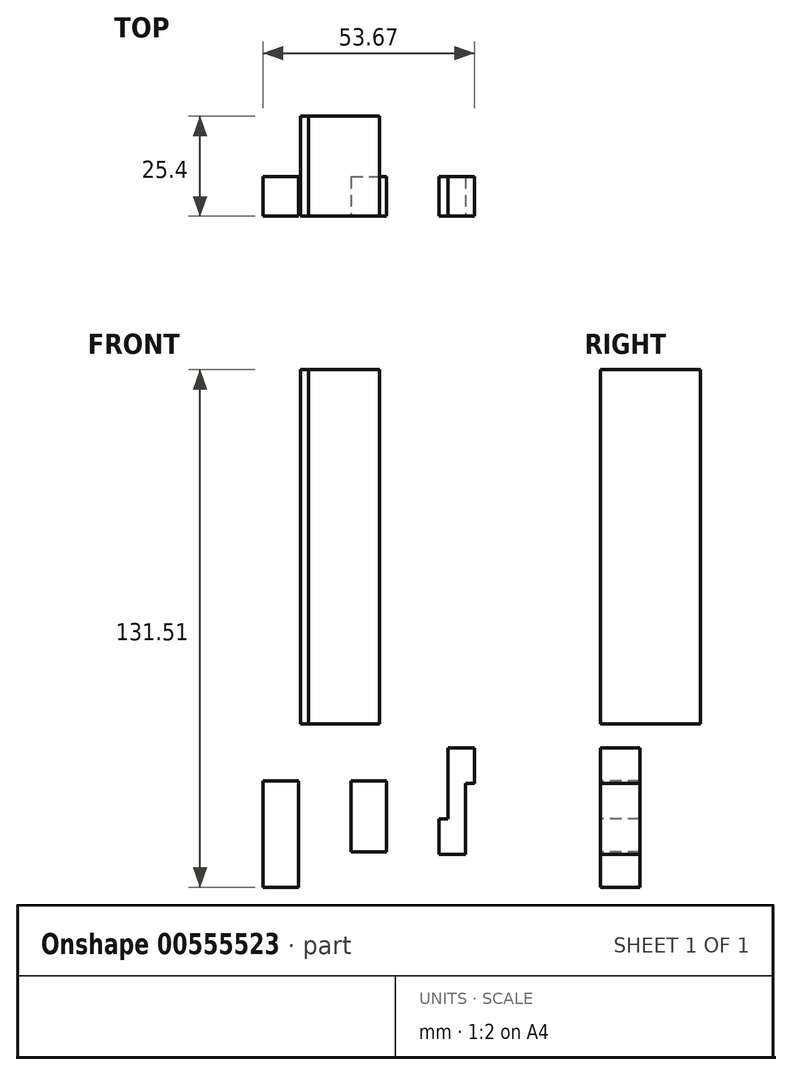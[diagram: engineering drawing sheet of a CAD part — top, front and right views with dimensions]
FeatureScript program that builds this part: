
annotation { "Feature Type Name" : "Feature", "Feature Type Description" : "" }
export const myFeature = defineFeature(function(context is Context, id is Id, definition is map)
    precondition{}
    {
        {
            var Q0;
            Q0=qCreatedBy(makeId("Front.planeOp"),FACE);
            var sketch = newSketch(context, id + "F0", { "sketchPlane" : qUnion([Q0])});
            skLineSegment(sketch, "E0.bottom", {"start": v(15.33, -10.42) * mm, "end": v(24.33, -10.42) * mm});
            skLineSegment(sketch, "E0.top", {"start": v(15.33, -37.42) * mm, "end": v(24.33, -37.42) * mm});
            skLineSegment(sketch, "E0.left", {"start": v(15.33, -10.42) * mm, "end": v(15.33, -37.42) * mm});
            skLineSegment(sketch, "E0.right", {"start": v(24.33, -10.42) * mm, "end": v(24.33, -37.42) * mm});
            skLineSegment(sketch, "E1.0", {"start": v(15.78, -10.42) * mm, "end": v(15.78, -37.42) * mm, "construction": true});
            skLineSegment(sketch, "E2.0", {"start": v(16.23, -10.42) * mm, "end": v(16.23, -37.42) * mm, "construction": true});
            skLineSegment(sketch, "E3.0", {"start": v(16.68, -10.42) * mm, "end": v(16.68, -37.42) * mm, "construction": true});
            skLineSegment(sketch, "E4.0", {"start": v(17.13, -10.42) * mm, "end": v(17.13, -37.42) * mm, "construction": true});
            skLineSegment(sketch, "E5.0", {"start": v(17.58, -10.42) * mm, "end": v(17.58, -37.42) * mm, "construction": true});
            skLineSegment(sketch, "E6.0", {"start": v(18.03, -10.42) * mm, "end": v(18.03, -37.42) * mm, "construction": true});
            skLineSegment(sketch, "E7.0", {"start": v(18.48, -10.42) * mm, "end": v(18.48, -37.42) * mm, "construction": true});
            skLineSegment(sketch, "E8.0", {"start": v(18.93, -10.42) * mm, "end": v(18.93, -37.42) * mm, "construction": true});
            skLineSegment(sketch, "E9.0", {"start": v(19.38, -10.42) * mm, "end": v(19.38, -37.42) * mm, "construction": true});
            skLineSegment(sketch, "E10.0", {"start": v(19.83, -10.42) * mm, "end": v(19.83, -37.42) * mm, "construction": true});
            skLineSegment(sketch, "E11.0", {"start": v(20.28, -10.42) * mm, "end": v(20.28, -37.42) * mm, "construction": true});
            skLineSegment(sketch, "E12.0", {"start": v(20.73, -10.42) * mm, "end": v(20.73, -37.42) * mm, "construction": true});
            skLineSegment(sketch, "E13.0", {"start": v(21.18, -10.42) * mm, "end": v(21.18, -37.42) * mm, "construction": true});
            skLineSegment(sketch, "E14.0", {"start": v(21.63, -10.42) * mm, "end": v(21.63, -37.42) * mm, "construction": true});
            skLineSegment(sketch, "E15.0", {"start": v(22.08, -10.42) * mm, "end": v(22.08, -37.42) * mm, "construction": true});
            skLineSegment(sketch, "E16.0", {"start": v(22.53, -10.42) * mm, "end": v(22.53, -37.42) * mm, "construction": true});
            skLineSegment(sketch, "E17.0", {"start": v(22.98, -10.42) * mm, "end": v(22.98, -37.42) * mm, "construction": true});
            skLineSegment(sketch, "E18.0", {"start": v(23.43, -10.42) * mm, "end": v(23.43, -37.42) * mm, "construction": true});
            skLineSegment(sketch, "E19.0", {"start": v(23.88, -10.42) * mm, "end": v(23.88, -37.42) * mm, "construction": true});
            skLineSegment(sketch, "E20.0", {"start": v(15.33, -36.97) * mm, "end": v(24.33, -36.97) * mm, "construction": true});
            skLineSegment(sketch, "E21.0", {"start": v(15.33, -36.52) * mm, "end": v(24.33, -36.52) * mm, "construction": true});
            skLineSegment(sketch, "E22.0", {"start": v(15.33, -36.07) * mm, "end": v(24.33, -36.07) * mm, "construction": true});
            skLineSegment(sketch, "E23.0", {"start": v(15.33, -35.62) * mm, "end": v(24.33, -35.62) * mm, "construction": true});
            skLineSegment(sketch, "E24.0", {"start": v(15.33, -35.17) * mm, "end": v(24.33, -35.17) * mm, "construction": true});
            skLineSegment(sketch, "E25.0", {"start": v(15.33, -34.72) * mm, "end": v(24.33, -34.72) * mm, "construction": true});
            skLineSegment(sketch, "E26.0", {"start": v(15.33, -34.27) * mm, "end": v(24.33, -34.27) * mm, "construction": true});
            skLineSegment(sketch, "E27.0", {"start": v(15.33, -33.82) * mm, "end": v(24.33, -33.82) * mm, "construction": true});
            skLineSegment(sketch, "E28.0", {"start": v(15.33, -33.37) * mm, "end": v(24.33, -33.37) * mm, "construction": true});
            skLineSegment(sketch, "E29.0", {"start": v(15.33, -32.92) * mm, "end": v(24.33, -32.92) * mm, "construction": true});
            skLineSegment(sketch, "E30.0", {"start": v(15.33, -32.47) * mm, "end": v(24.33, -32.47) * mm, "construction": true});
            skLineSegment(sketch, "E31.0", {"start": v(15.33, -32.02) * mm, "end": v(24.33, -32.02) * mm, "construction": true});
            skLineSegment(sketch, "E32.0", {"start": v(15.33, -31.57) * mm, "end": v(24.33, -31.57) * mm, "construction": true});
            skLineSegment(sketch, "E33.0", {"start": v(15.33, -31.12) * mm, "end": v(24.33, -31.12) * mm, "construction": true});
            skLineSegment(sketch, "E34.0", {"start": v(15.33, -30.67) * mm, "end": v(24.33, -30.67) * mm, "construction": true});
            skLineSegment(sketch, "E35.0", {"start": v(15.33, -30.22) * mm, "end": v(24.33, -30.22) * mm, "construction": true});
            skLineSegment(sketch, "E36.0", {"start": v(15.33, -29.77) * mm, "end": v(24.33, -29.77) * mm, "construction": true});
            skLineSegment(sketch, "E37.0", {"start": v(15.33, -29.32) * mm, "end": v(24.33, -29.32) * mm, "construction": true});
            skLineSegment(sketch, "E38.0", {"start": v(15.33, -28.87) * mm, "end": v(24.33, -28.87) * mm, "construction": true});
            skLineSegment(sketch, "E39.0", {"start": v(15.33, -28.42) * mm, "end": v(24.33, -28.42) * mm, "construction": true});
            skLineSegment(sketch, "E40.0", {"start": v(15.33, -27.97) * mm, "end": v(24.33, -27.97) * mm, "construction": true});
            skLineSegment(sketch, "E41.0", {"start": v(15.33, -27.52) * mm, "end": v(24.33, -27.52) * mm, "construction": true});
            skLineSegment(sketch, "E42.0", {"start": v(15.33, -27.07) * mm, "end": v(24.33, -27.07) * mm, "construction": true});
            skLineSegment(sketch, "E43.0", {"start": v(15.33, -26.62) * mm, "end": v(24.33, -26.62) * mm, "construction": true});
            skLineSegment(sketch, "E44.0", {"start": v(15.33, -26.17) * mm, "end": v(24.33, -26.17) * mm, "construction": true});
            skLineSegment(sketch, "E45.0", {"start": v(15.33, -25.72) * mm, "end": v(24.33, -25.72) * mm, "construction": true});
            skLineSegment(sketch, "E46.0", {"start": v(15.33, -25.27) * mm, "end": v(24.33, -25.27) * mm, "construction": true});
            skLineSegment(sketch, "E47.0", {"start": v(15.33, -24.82) * mm, "end": v(24.33, -24.82) * mm, "construction": true});
            skLineSegment(sketch, "E48.0", {"start": v(15.33, -24.37) * mm, "end": v(24.33, -24.37) * mm, "construction": true});
            skLineSegment(sketch, "E49.0", {"start": v(15.33, -23.92) * mm, "end": v(24.33, -23.92) * mm, "construction": true});
            skLineSegment(sketch, "E50.0", {"start": v(15.33, -23.47) * mm, "end": v(24.33, -23.47) * mm, "construction": true});
            skLineSegment(sketch, "E51.0", {"start": v(15.33, -23.02) * mm, "end": v(24.33, -23.02) * mm, "construction": true});
            skLineSegment(sketch, "E52.0", {"start": v(15.33, -22.57) * mm, "end": v(24.33, -22.57) * mm, "construction": true});
            skLineSegment(sketch, "E53.0", {"start": v(15.33, -22.12) * mm, "end": v(24.33, -22.12) * mm, "construction": true});
            skLineSegment(sketch, "E54.0", {"start": v(15.33, -21.67) * mm, "end": v(24.33, -21.67) * mm, "construction": true});
            skLineSegment(sketch, "E55.0", {"start": v(15.33, -21.22) * mm, "end": v(24.33, -21.22) * mm, "construction": true});
            skLineSegment(sketch, "E56.0", {"start": v(15.33, -20.77) * mm, "end": v(24.33, -20.77) * mm, "construction": true});
            skLineSegment(sketch, "E57.0", {"start": v(15.33, -20.32) * mm, "end": v(24.33, -20.32) * mm, "construction": true});
            skLineSegment(sketch, "E58.0", {"start": v(15.33, -19.87) * mm, "end": v(24.33, -19.87) * mm, "construction": true});
            skLineSegment(sketch, "E59.0", {"start": v(15.33, -19.42) * mm, "end": v(24.33, -19.42) * mm, "construction": true});
            skLineSegment(sketch, "E60.0", {"start": v(15.33, -18.97) * mm, "end": v(24.33, -18.97) * mm, "construction": true});
            skLineSegment(sketch, "E61.0", {"start": v(15.33, -18.52) * mm, "end": v(24.33, -18.52) * mm, "construction": true});
            skLineSegment(sketch, "E62.0", {"start": v(15.33, -18.07) * mm, "end": v(24.33, -18.07) * mm, "construction": true});
            skLineSegment(sketch, "E63.0", {"start": v(15.33, -17.62) * mm, "end": v(24.33, -17.62) * mm, "construction": true});
            skLineSegment(sketch, "E64.0", {"start": v(15.33, -17.17) * mm, "end": v(24.33, -17.17) * mm, "construction": true});
            skLineSegment(sketch, "E65.0", {"start": v(15.33, -16.72) * mm, "end": v(24.33, -16.72) * mm, "construction": true});
            skLineSegment(sketch, "E66.0", {"start": v(15.33, -16.27) * mm, "end": v(24.33, -16.27) * mm, "construction": true});
            skLineSegment(sketch, "E67.0", {"start": v(15.33, -15.82) * mm, "end": v(24.33, -15.82) * mm, "construction": true});
            skLineSegment(sketch, "E68.0", {"start": v(15.33, -15.37) * mm, "end": v(24.33, -15.37) * mm, "construction": true});
            skLineSegment(sketch, "E69.0", {"start": v(15.33, -14.92) * mm, "end": v(24.33, -14.92) * mm, "construction": true});
            skLineSegment(sketch, "E70.0", {"start": v(15.33, -14.47) * mm, "end": v(24.33, -14.47) * mm, "construction": true});
            skLineSegment(sketch, "E71.0", {"start": v(15.33, -14.02) * mm, "end": v(24.33, -14.02) * mm, "construction": true});
            skLineSegment(sketch, "E72.0", {"start": v(15.33, -13.57) * mm, "end": v(24.33, -13.57) * mm, "construction": true});
            skLineSegment(sketch, "E73.0", {"start": v(15.33, -13.12) * mm, "end": v(24.33, -13.12) * mm, "construction": true});
            skLineSegment(sketch, "E74.0", {"start": v(15.33, -12.67) * mm, "end": v(24.33, -12.67) * mm, "construction": true});
            skLineSegment(sketch, "E75.0", {"start": v(15.33, -12.22) * mm, "end": v(24.33, -12.22) * mm, "construction": true});
            skLineSegment(sketch, "E76.0", {"start": v(15.33, -11.77) * mm, "end": v(24.33, -11.77) * mm, "construction": true});
            skLineSegment(sketch, "E77.0", {"start": v(15.33, -11.32) * mm, "end": v(24.33, -11.32) * mm, "construction": true});
            skLineSegment(sketch, "E78.0", {"start": v(15.33, -10.87) * mm, "end": v(24.33, -10.87) * mm, "construction": true});
            skSolve(sketch);
        }
        {
            var Q0;
            Q0=makeQuery(id+"F0.imprint","IMPRINT",FACE,{"disambiguationData":[TD([[makeQuery(id+"F0.imprint","IMPRINT",EDGE,{"derivedFrom":sQuery(id+"F0.wireOp",EDGE,"E0.bottom")}),-1.0]])]});
            extrude(context, id + "F1", {"entities" : qUnion([Q0]), "oppositeDirection" : true, "depth" : 10 * mm, "offsetDistance" : 25.4 * mm});
        }
        {
            var Q0;
            Q0=qCreatedBy(makeId("Front.planeOp"),FACE);
            var sketch = newSketch(context, id + "F2", { "sketchPlane" : qUnion([Q0])});
            skLineSegment(sketch, "E79.top", {"start": v(37.66, -28.43) * mm, "end": v(46.66, -28.43) * mm});
            skLineSegment(sketch, "E80.0", {"start": v(38.11, -10.43) * mm, "end": v(38.11, -28.43) * mm, "construction": true});
            skLineSegment(sketch, "E81.0", {"start": v(38.56, -10.43) * mm, "end": v(38.56, -28.43) * mm, "construction": true});
            skLineSegment(sketch, "E82.0", {"start": v(39.01, -10.43) * mm, "end": v(39.01, -28.43) * mm, "construction": true});
            skLineSegment(sketch, "E83.0", {"start": v(39.46, -10.43) * mm, "end": v(39.46, -28.43) * mm, "construction": true});
            skLineSegment(sketch, "E84.0", {"start": v(39.91, -10.43) * mm, "end": v(39.91, -28.43) * mm, "construction": true});
            skLineSegment(sketch, "E85.0", {"start": v(40.36, -10.43) * mm, "end": v(40.36, -28.43) * mm, "construction": true});
            skLineSegment(sketch, "E86.0", {"start": v(40.81, -10.43) * mm, "end": v(40.81, -28.43) * mm, "construction": true});
            skLineSegment(sketch, "E87.0", {"start": v(41.26, -10.43) * mm, "end": v(41.26, -28.43) * mm, "construction": true});
            skLineSegment(sketch, "E88.0", {"start": v(41.71, -10.43) * mm, "end": v(41.71, -28.43) * mm, "construction": true});
            skLineSegment(sketch, "E89.0", {"start": v(42.16, -10.43) * mm, "end": v(42.16, -28.43) * mm, "construction": true});
            skLineSegment(sketch, "E90.0", {"start": v(42.61, -10.43) * mm, "end": v(42.61, -28.43) * mm, "construction": true});
            skLineSegment(sketch, "E91.0", {"start": v(43.06, -10.43) * mm, "end": v(43.06, -28.43) * mm, "construction": true});
            skLineSegment(sketch, "E92.0", {"start": v(43.51, -10.43) * mm, "end": v(43.51, -28.43) * mm, "construction": true});
            skLineSegment(sketch, "E93.0", {"start": v(43.96, -10.43) * mm, "end": v(43.96, -28.43) * mm, "construction": true});
            skLineSegment(sketch, "E94.0", {"start": v(44.41, -10.43) * mm, "end": v(44.41, -28.43) * mm, "construction": true});
            skLineSegment(sketch, "E95.0", {"start": v(44.86, -10.43) * mm, "end": v(44.86, -28.43) * mm, "construction": true});
            skLineSegment(sketch, "E96.0", {"start": v(45.31, -10.43) * mm, "end": v(45.31, -28.43) * mm, "construction": true});
            skLineSegment(sketch, "E97.0", {"start": v(45.76, -10.43) * mm, "end": v(45.76, -28.43) * mm, "construction": true});
            skLineSegment(sketch, "E98.0", {"start": v(46.21, -10.43) * mm, "end": v(46.21, -28.43) * mm, "construction": true});
            skLineSegment(sketch, "E99.0", {"start": v(37.66, -27.98) * mm, "end": v(46.66, -27.98) * mm, "construction": true});
            skLineSegment(sketch, "E100.0", {"start": v(37.66, -27.53) * mm, "end": v(46.66, -27.53) * mm, "construction": true});
            skLineSegment(sketch, "E101.0", {"start": v(37.66, -27.08) * mm, "end": v(46.66, -27.08) * mm, "construction": true});
            skLineSegment(sketch, "E102.0", {"start": v(37.66, -26.63) * mm, "end": v(46.66, -26.63) * mm, "construction": true});
            skLineSegment(sketch, "E103.0", {"start": v(37.66, -26.18) * mm, "end": v(46.66, -26.18) * mm, "construction": true});
            skLineSegment(sketch, "E104.0", {"start": v(37.66, -25.73) * mm, "end": v(46.66, -25.73) * mm, "construction": true});
            skLineSegment(sketch, "E105.0", {"start": v(37.66, -25.28) * mm, "end": v(46.66, -25.28) * mm, "construction": true});
            skLineSegment(sketch, "E106.0", {"start": v(37.66, -24.83) * mm, "end": v(46.66, -24.83) * mm, "construction": true});
            skLineSegment(sketch, "E107.0", {"start": v(37.66, -24.38) * mm, "end": v(46.66, -24.38) * mm, "construction": true});
            skLineSegment(sketch, "E108.0", {"start": v(37.66, -23.93) * mm, "end": v(46.66, -23.93) * mm, "construction": true});
            skLineSegment(sketch, "E109.0", {"start": v(37.66, -23.48) * mm, "end": v(46.66, -23.48) * mm, "construction": true});
            skLineSegment(sketch, "E110.0", {"start": v(37.66, -23.03) * mm, "end": v(46.66, -23.03) * mm, "construction": true});
            skLineSegment(sketch, "E111.0", {"start": v(37.66, -22.58) * mm, "end": v(46.66, -22.58) * mm, "construction": true});
            skLineSegment(sketch, "E112.0", {"start": v(37.66, -22.13) * mm, "end": v(46.66, -22.13) * mm, "construction": true});
            skLineSegment(sketch, "E113.0", {"start": v(37.66, -21.68) * mm, "end": v(46.66, -21.68) * mm, "construction": true});
            skLineSegment(sketch, "E114.0", {"start": v(37.66, -21.23) * mm, "end": v(46.66, -21.23) * mm, "construction": true});
            skLineSegment(sketch, "E115.0", {"start": v(37.66, -20.78) * mm, "end": v(46.66, -20.78) * mm, "construction": true});
            skLineSegment(sketch, "E116.0", {"start": v(37.66, -20.33) * mm, "end": v(46.66, -20.33) * mm, "construction": true});
            skLineSegment(sketch, "E117.0", {"start": v(37.66, -19.88) * mm, "end": v(46.66, -19.88) * mm, "construction": true});
            skLineSegment(sketch, "E118.0", {"start": v(37.66, -19.43) * mm, "end": v(46.66, -19.43) * mm, "construction": true});
            skLineSegment(sketch, "E119.0", {"start": v(37.66, -18.98) * mm, "end": v(46.66, -18.98) * mm, "construction": true});
            skLineSegment(sketch, "E120.0", {"start": v(37.66, -18.53) * mm, "end": v(46.66, -18.53) * mm, "construction": true});
            skLineSegment(sketch, "E121.0", {"start": v(37.66, -18.08) * mm, "end": v(46.66, -18.08) * mm, "construction": true});
            skLineSegment(sketch, "E122.0", {"start": v(37.66, -17.63) * mm, "end": v(46.66, -17.63) * mm, "construction": true});
            skLineSegment(sketch, "E123.0", {"start": v(37.66, -17.18) * mm, "end": v(46.66, -17.18) * mm, "construction": true});
            skLineSegment(sketch, "E124.0", {"start": v(37.66, -16.73) * mm, "end": v(46.66, -16.73) * mm, "construction": true});
            skLineSegment(sketch, "E125.0", {"start": v(37.66, -16.28) * mm, "end": v(46.66, -16.28) * mm, "construction": true});
            skLineSegment(sketch, "E126.0", {"start": v(37.66, -15.83) * mm, "end": v(46.66, -15.83) * mm, "construction": true});
            skLineSegment(sketch, "E127.0", {"start": v(37.66, -15.38) * mm, "end": v(46.66, -15.38) * mm, "construction": true});
            skLineSegment(sketch, "E128.0", {"start": v(37.66, -14.93) * mm, "end": v(46.66, -14.93) * mm, "construction": true});
            skLineSegment(sketch, "E129.0", {"start": v(37.66, -14.48) * mm, "end": v(46.66, -14.48) * mm, "construction": true});
            skLineSegment(sketch, "E130.0", {"start": v(37.66, -14.03) * mm, "end": v(46.66, -14.03) * mm, "construction": true});
            skLineSegment(sketch, "E131.0", {"start": v(37.66, -13.58) * mm, "end": v(46.66, -13.58) * mm, "construction": true});
            skLineSegment(sketch, "E132.0", {"start": v(37.66, -13.13) * mm, "end": v(46.66, -13.13) * mm, "construction": true});
            skLineSegment(sketch, "E133.0", {"start": v(37.66, -12.68) * mm, "end": v(46.66, -12.68) * mm, "construction": true});
            skLineSegment(sketch, "E134.0", {"start": v(37.66, -12.23) * mm, "end": v(46.66, -12.23) * mm, "construction": true});
            skLineSegment(sketch, "E135.0", {"start": v(37.66, -11.78) * mm, "end": v(46.66, -11.78) * mm, "construction": true});
            skLineSegment(sketch, "E136.0", {"start": v(37.66, -11.33) * mm, "end": v(46.66, -11.33) * mm, "construction": true});
            skLineSegment(sketch, "E137.0", {"start": v(37.66, -10.88) * mm, "end": v(46.66, -10.88) * mm, "construction": true});
            skLineSegment(sketch, "E138.0", {"start": v(37.66, -10.43) * mm, "end": v(46.66, -10.43) * mm});
            skLineSegment(sketch, "E139", {"start": v(37.66, -28.43) * mm, "end": v(37.66, -10.43) * mm});
            skLineSegment(sketch, "E140", {"start": v(46.66, -10.43) * mm, "end": v(46.66, -28.43) * mm});
            skSolve(sketch);
        }
        {
            var Q0;
            Q0 = qSketchRegion(id + "F2", true);
            extrude(context, id + "F3", {"entities" : qUnion([Q0]), "oppositeDirection" : true, "depth" : 10 * mm, "offsetDistance" : 25.4 * mm});
        }
        {
            var Q0;
            Q0=qCreatedBy(makeId("Front.planeOp"),FACE);
            var sketch = newSketch(context, id + "F4", { "sketchPlane" : qUnion([Q0])});
            skLineSegment(sketch, "E141.0", {"start": v(62.25, -2.04) * mm, "end": v(62.25, -29.04) * mm, "construction": true});
            skLineSegment(sketch, "E142.0", {"start": v(62.7, -2.04) * mm, "end": v(62.7, -29.04) * mm, "construction": true});
            skLineSegment(sketch, "E143.0", {"start": v(63.15, -2.04) * mm, "end": v(63.15, -29.04) * mm, "construction": true});
            skLineSegment(sketch, "E144.0", {"start": v(63.6, -2.04) * mm, "end": v(63.6, -29.04) * mm, "construction": true});
            skLineSegment(sketch, "E145.0", {"start": v(64.05, -2.04) * mm, "end": v(64.05, -29.04) * mm, "construction": true});
            skLineSegment(sketch, "E146.0", {"start": v(64.5, -2.04) * mm, "end": v(64.5, -29.04) * mm, "construction": true});
            skLineSegment(sketch, "E147.0", {"start": v(64.95, -2.04) * mm, "end": v(64.95, -29.04) * mm, "construction": true});
            skLineSegment(sketch, "E148.0", {"start": v(65.4, -2.04) * mm, "end": v(65.4, -29.04) * mm, "construction": true});
            skLineSegment(sketch, "E149.0", {"start": v(65.85, -2.04) * mm, "end": v(65.85, -29.04) * mm, "construction": true});
            skLineSegment(sketch, "E150.0", {"start": v(66.3, -2.04) * mm, "end": v(66.3, -29.04) * mm, "construction": true});
            skLineSegment(sketch, "E151.0", {"start": v(66.75, -2.04) * mm, "end": v(66.75, -29.04) * mm, "construction": true});
            skLineSegment(sketch, "E152.0", {"start": v(67.2, -2.04) * mm, "end": v(67.2, -11.04) * mm, "construction": true});
            skLineSegment(sketch, "E153.0", {"start": v(67.65, -2.04) * mm, "end": v(67.65, -11.04) * mm, "construction": true});
            skLineSegment(sketch, "E154.0", {"start": v(68.1, -2.04) * mm, "end": v(68.1, -11.04) * mm, "construction": true});
            skLineSegment(sketch, "E155.0", {"start": v(68.55, -2.04) * mm, "end": v(68.55, -11.04) * mm, "construction": true});
            skLineSegment(sketch, "E156.0", {"start": v(60, -28.59) * mm, "end": v(66.75, -28.59) * mm, "construction": true});
            skLineSegment(sketch, "E157.0", {"start": v(60, -28.14) * mm, "end": v(66.75, -28.14) * mm, "construction": true});
            skLineSegment(sketch, "E158.0", {"start": v(60, -27.69) * mm, "end": v(66.75, -27.69) * mm, "construction": true});
            skLineSegment(sketch, "E159.0", {"start": v(60, -27.24) * mm, "end": v(66.75, -27.24) * mm, "construction": true});
            skLineSegment(sketch, "E160.0", {"start": v(60, -26.79) * mm, "end": v(66.75, -26.79) * mm, "construction": true});
            skLineSegment(sketch, "E161.0", {"start": v(60, -26.34) * mm, "end": v(66.75, -26.34) * mm, "construction": true});
            skLineSegment(sketch, "E162.0", {"start": v(60, -25.89) * mm, "end": v(66.75, -25.89) * mm, "construction": true});
            skLineSegment(sketch, "E163.0", {"start": v(60, -25.44) * mm, "end": v(66.75, -25.44) * mm, "construction": true});
            skLineSegment(sketch, "E164.0", {"start": v(60, -24.99) * mm, "end": v(66.75, -24.99) * mm, "construction": true});
            skLineSegment(sketch, "E165.0", {"start": v(60, -24.54) * mm, "end": v(66.75, -24.54) * mm, "construction": true});
            skLineSegment(sketch, "E166.0", {"start": v(60, -24.09) * mm, "end": v(66.75, -24.09) * mm, "construction": true});
            skLineSegment(sketch, "E167.0", {"start": v(60, -23.64) * mm, "end": v(66.75, -23.64) * mm, "construction": true});
            skLineSegment(sketch, "E168.0", {"start": v(60, -23.19) * mm, "end": v(66.75, -23.19) * mm, "construction": true});
            skLineSegment(sketch, "E169.0", {"start": v(60, -22.74) * mm, "end": v(66.75, -22.74) * mm, "construction": true});
            skLineSegment(sketch, "E170.0", {"start": v(60, -22.29) * mm, "end": v(66.75, -22.29) * mm, "construction": true});
            skLineSegment(sketch, "E171.0", {"start": v(60, -21.84) * mm, "end": v(66.75, -21.84) * mm, "construction": true});
            skLineSegment(sketch, "E172.0", {"start": v(60, -21.39) * mm, "end": v(66.75, -21.39) * mm, "construction": true});
            skLineSegment(sketch, "E173.0", {"start": v(60, -20.94) * mm, "end": v(66.75, -20.94) * mm, "construction": true});
            skLineSegment(sketch, "E174.0", {"start": v(60, -20.49) * mm, "end": v(66.75, -20.49) * mm, "construction": true});
            skLineSegment(sketch, "E175.0", {"start": v(60, -20.04) * mm, "end": v(66.75, -20.04) * mm, "construction": true});
            skLineSegment(sketch, "E176.0", {"start": v(62.25, -19.59) * mm, "end": v(66.75, -19.59) * mm, "construction": true});
            skLineSegment(sketch, "E177.0", {"start": v(62.25, -19.14) * mm, "end": v(66.75, -19.14) * mm, "construction": true});
            skLineSegment(sketch, "E178.0", {"start": v(62.25, -18.69) * mm, "end": v(66.75, -18.69) * mm, "construction": true});
            skLineSegment(sketch, "E179.0", {"start": v(62.25, -18.24) * mm, "end": v(66.75, -18.24) * mm, "construction": true});
            skLineSegment(sketch, "E180.0", {"start": v(62.25, -17.79) * mm, "end": v(66.75, -17.79) * mm, "construction": true});
            skLineSegment(sketch, "E181.0", {"start": v(62.25, -17.34) * mm, "end": v(66.75, -17.34) * mm, "construction": true});
            skLineSegment(sketch, "E182.0", {"start": v(62.25, -16.89) * mm, "end": v(66.75, -16.89) * mm, "construction": true});
            skLineSegment(sketch, "E183.0", {"start": v(62.25, -16.44) * mm, "end": v(66.75, -16.44) * mm, "construction": true});
            skLineSegment(sketch, "E184.0", {"start": v(62.25, -15.99) * mm, "end": v(66.75, -15.99) * mm, "construction": true});
            skLineSegment(sketch, "E185.0", {"start": v(62.25, -15.54) * mm, "end": v(66.75, -15.54) * mm, "construction": true});
            skLineSegment(sketch, "E186.0", {"start": v(62.25, -15.09) * mm, "end": v(66.75, -15.09) * mm, "construction": true});
            skLineSegment(sketch, "E187.0", {"start": v(62.25, -14.64) * mm, "end": v(66.75, -14.64) * mm, "construction": true});
            skLineSegment(sketch, "E188.0", {"start": v(62.25, -14.19) * mm, "end": v(66.75, -14.19) * mm, "construction": true});
            skLineSegment(sketch, "E189.0", {"start": v(62.25, -13.74) * mm, "end": v(66.75, -13.74) * mm, "construction": true});
            skLineSegment(sketch, "E190.0", {"start": v(62.25, -13.29) * mm, "end": v(66.75, -13.29) * mm, "construction": true});
            skLineSegment(sketch, "E191.0", {"start": v(62.25, -12.84) * mm, "end": v(66.75, -12.84) * mm, "construction": true});
            skLineSegment(sketch, "E192.0", {"start": v(62.25, -12.39) * mm, "end": v(66.75, -12.39) * mm, "construction": true});
            skLineSegment(sketch, "E193.0", {"start": v(62.25, -11.94) * mm, "end": v(66.75, -11.94) * mm, "construction": true});
            skLineSegment(sketch, "E194.0", {"start": v(62.25, -11.49) * mm, "end": v(66.75, -11.49) * mm, "construction": true});
            skLineSegment(sketch, "E195.0", {"start": v(62.25, -11.04) * mm, "end": v(69, -11.04) * mm, "construction": true});
            skLineSegment(sketch, "E196.0", {"start": v(62.25, -10.59) * mm, "end": v(69, -10.59) * mm, "construction": true});
            skLineSegment(sketch, "E197.0", {"start": v(62.25, -10.14) * mm, "end": v(69, -10.14) * mm, "construction": true});
            skLineSegment(sketch, "E198.0", {"start": v(62.25, -9.69) * mm, "end": v(69, -9.69) * mm, "construction": true});
            skLineSegment(sketch, "E199.0", {"start": v(62.25, -9.24) * mm, "end": v(69, -9.24) * mm, "construction": true});
            skLineSegment(sketch, "E200.0", {"start": v(62.25, -8.79) * mm, "end": v(69, -8.79) * mm, "construction": true});
            skLineSegment(sketch, "E201.0", {"start": v(62.25, -8.34) * mm, "end": v(69, -8.34) * mm, "construction": true});
            skLineSegment(sketch, "E202.0", {"start": v(62.25, -7.89) * mm, "end": v(69, -7.89) * mm, "construction": true});
            skLineSegment(sketch, "E203.0", {"start": v(62.25, -7.44) * mm, "end": v(69, -7.44) * mm, "construction": true});
            skLineSegment(sketch, "E204.0", {"start": v(62.25, -6.99) * mm, "end": v(69, -6.99) * mm, "construction": true});
            skLineSegment(sketch, "E205.0", {"start": v(62.25, -6.54) * mm, "end": v(69, -6.54) * mm, "construction": true});
            skLineSegment(sketch, "E206.0", {"start": v(62.25, -6.09) * mm, "end": v(69, -6.09) * mm, "construction": true});
            skLineSegment(sketch, "E207.0", {"start": v(62.25, -5.64) * mm, "end": v(69, -5.64) * mm, "construction": true});
            skLineSegment(sketch, "E208.0", {"start": v(62.25, -5.19) * mm, "end": v(69, -5.19) * mm, "construction": true});
            skLineSegment(sketch, "E209.0", {"start": v(62.25, -4.74) * mm, "end": v(69, -4.74) * mm, "construction": true});
            skLineSegment(sketch, "E210.0", {"start": v(62.25, -4.29) * mm, "end": v(69, -4.29) * mm, "construction": true});
            skLineSegment(sketch, "E211.0", {"start": v(62.25, -3.84) * mm, "end": v(69, -3.84) * mm, "construction": true});
            skLineSegment(sketch, "E212.0", {"start": v(62.25, -3.39) * mm, "end": v(69, -3.39) * mm, "construction": true});
            skLineSegment(sketch, "E213.0", {"start": v(62.25, -2.94) * mm, "end": v(69, -2.94) * mm, "construction": true});
            skLineSegment(sketch, "E214.0", {"start": v(62.25, -2.49) * mm, "end": v(69, -2.49) * mm, "construction": true});
            skLineSegment(sketch, "E215", {"start": v(60, -29.04) * mm, "end": v(60, -20.04) * mm});
            skLineSegment(sketch, "E216", {"start": v(60, -20.04) * mm, "end": v(62.25, -20.04) * mm});
            skLineSegment(sketch, "E217", {"start": v(62.25, -20.04) * mm, "end": v(62.25, -2.04) * mm});
            skLineSegment(sketch, "E218.trimOffspring", {"start": v(60.45, -20.04) * mm, "end": v(60.45, -29.04) * mm, "construction": true});
            skLineSegment(sketch, "E219.trimOffspring", {"start": v(60.9, -20.04) * mm, "end": v(60.9, -29.04) * mm, "construction": true});
            skLineSegment(sketch, "E220.trimOffspring", {"start": v(61.35, -20.04) * mm, "end": v(61.35, -29.04) * mm, "construction": true});
            skLineSegment(sketch, "E221.trimOffspring", {"start": v(61.8, -20.04) * mm, "end": v(61.8, -29.04) * mm, "construction": true});
            skLineSegment(sketch, "E222", {"start": v(62.25, -2.04) * mm, "end": v(69, -2.04) * mm});
            skLineSegment(sketch, "E223", {"start": v(60, -29.04) * mm, "end": v(66.75, -29.04) * mm});
            skLineSegment(sketch, "E224", {"start": v(66.75, -29.04) * mm, "end": v(66.75, -11.04) * mm});
            skLineSegment(sketch, "E225", {"start": v(66.75, -11.04) * mm, "end": v(69, -11.04) * mm});
            skLineSegment(sketch, "E226", {"start": v(69, -2.04) * mm, "end": v(69, -11.04) * mm});
            skSolve(sketch);
        }
        {
            var Q0;
            Q0=makeQuery(id+"F4.imprint","IMPRINT",FACE,{"disambiguationData":[TD([[makeQuery(id+"F4.imprint","IMPRINT",EDGE,{"derivedFrom":sQuery(id+"F4.wireOp",EDGE,"E215")}),-1.0]])]});
            extrude(context, id + "F5", {"entities" : qUnion([Q0]), "oppositeDirection" : true, "depth" : 10 * mm, "offsetDistance" : 25.4 * mm});
        }
        {
            var Q0;
            Q0=makeQuery(id+"F2.imprint","IMPRINT",FACE,{"disambiguationData":[TD([[makeQuery(id+"F2.imprint","IMPRINT",EDGE,{"derivedFrom":sQuery(id+"F2.wireOp",EDGE,"E79.top")}),1.0]])]});
            var sketch = newSketch(context, id + "F6", { "sketchPlane" : qUnion([Q0])});
            skLineSegment(sketch, "E227.0.1.0", {"start": v(26.84, 6.1) * mm, "end": v(44.84, 6.1) * mm, "construction": true});
            skLineSegment(sketch, "E227.0.2.0", {"start": v(26.83, 8.1) * mm, "end": v(44.83, 8.1) * mm, "construction": true});
            skLineSegment(sketch, "E227.0.3.0", {"start": v(26.83, 10.1) * mm, "end": v(44.83, 10.1) * mm, "construction": true});
            skLineSegment(sketch, "E227.0.4.0", {"start": v(26.83, 12.1) * mm, "end": v(44.83, 12.1) * mm, "construction": true});
            skLineSegment(sketch, "E227.0.5.0", {"start": v(26.83, 14.1) * mm, "end": v(44.83, 14.1) * mm, "construction": true});
            skLineSegment(sketch, "E227.0.6.0", {"start": v(26.83, 16.1) * mm, "end": v(44.83, 16.1) * mm, "construction": true});
            skLineSegment(sketch, "E227.0.7.0", {"start": v(26.83, 18.1) * mm, "end": v(44.83, 18.1) * mm, "construction": true});
            skLineSegment(sketch, "E227.0.8.0", {"start": v(26.83, 20.1) * mm, "end": v(44.83, 20.1) * mm, "construction": true});
            skLineSegment(sketch, "E227.0.9.0", {"start": v(26.83, 22.1) * mm, "end": v(44.83, 22.1) * mm, "construction": true});
            skLineSegment(sketch, "E227.0.10.0", {"start": v(26.83, 24.1) * mm, "end": v(44.83, 24.1) * mm, "construction": true});
            skLineSegment(sketch, "E227.0.11.0", {"start": v(26.83, 26.1) * mm, "end": v(44.83, 26.1) * mm, "construction": true});
            skLineSegment(sketch, "E227.0.12.0", {"start": v(26.83, 28.1) * mm, "end": v(44.83, 28.1) * mm, "construction": true});
            skLineSegment(sketch, "E227.0.13.0", {"start": v(26.83, 30.1) * mm, "end": v(44.83, 30.1) * mm, "construction": true});
            skLineSegment(sketch, "E227.0.14.0", {"start": v(26.83, 32.1) * mm, "end": v(44.83, 32.1) * mm, "construction": true});
            skLineSegment(sketch, "E227.0.15.0", {"start": v(26.83, 34.1) * mm, "end": v(44.83, 34.1) * mm, "construction": true});
            skLineSegment(sketch, "E227.0.16.0", {"start": v(26.83, 36.1) * mm, "end": v(44.83, 36.1) * mm, "construction": true});
            skLineSegment(sketch, "E227.0.17.0", {"start": v(26.83, 38.1) * mm, "end": v(44.83, 38.1) * mm, "construction": true});
            skLineSegment(sketch, "E227.0.18.0", {"start": v(26.83, 40.1) * mm, "end": v(44.83, 40.1) * mm, "construction": true});
            skLineSegment(sketch, "E227.0.19.0", {"start": v(26.83, 42.1) * mm, "end": v(44.83, 42.1) * mm, "construction": true});
            skLineSegment(sketch, "E227.0.20.0", {"start": v(26.83, 44.1) * mm, "end": v(44.83, 44.1) * mm, "construction": true});
            skLineSegment(sketch, "E227.0.21.0", {"start": v(26.83, 46.1) * mm, "end": v(44.83, 46.1) * mm, "construction": true});
            skLineSegment(sketch, "E227.0.22.0", {"start": v(26.83, 48.1) * mm, "end": v(44.83, 48.1) * mm, "construction": true});
            skLineSegment(sketch, "E227.0.23.0", {"start": v(26.83, 50.1) * mm, "end": v(44.83, 50.1) * mm, "construction": true});
            skLineSegment(sketch, "E227.0.24.0", {"start": v(26.83, 52.1) * mm, "end": v(44.83, 52.1) * mm, "construction": true});
            skLineSegment(sketch, "E227.0.25.0", {"start": v(26.83, 54.1) * mm, "end": v(44.83, 54.1) * mm, "construction": true});
            skLineSegment(sketch, "E227.0.26.0", {"start": v(26.83, 56.1) * mm, "end": v(44.83, 56.1) * mm, "construction": true});
            skLineSegment(sketch, "E227.0.27.0", {"start": v(26.83, 58.1) * mm, "end": v(44.83, 58.1) * mm, "construction": true});
            skLineSegment(sketch, "E227.0.28.0", {"start": v(26.83, 60.1) * mm, "end": v(44.83, 60.1) * mm, "construction": true});
            skLineSegment(sketch, "E227.0.29.0", {"start": v(26.83, 62.1) * mm, "end": v(44.83, 62.1) * mm, "construction": true});
            skLineSegment(sketch, "E227.0.30.0", {"start": v(26.83, 64.1) * mm, "end": v(44.83, 64.1) * mm, "construction": true});
            skLineSegment(sketch, "E227.0.31.0", {"start": v(26.83, 66.1) * mm, "end": v(44.83, 66.1) * mm, "construction": true});
            skLineSegment(sketch, "E227.0.32.0", {"start": v(26.83, 68.1) * mm, "end": v(44.83, 68.1) * mm, "construction": true});
            skLineSegment(sketch, "E227.0.33.0", {"start": v(26.83, 70.1) * mm, "end": v(44.83, 70.1) * mm, "construction": true});
            skLineSegment(sketch, "E227.0.34.0", {"start": v(26.83, 72.1) * mm, "end": v(44.83, 72.1) * mm, "construction": true});
            skLineSegment(sketch, "E227.0.35.0", {"start": v(26.83, 74.1) * mm, "end": v(44.83, 74.1) * mm, "construction": true});
            skLineSegment(sketch, "E227.0.36.0", {"start": v(26.83, 76.1) * mm, "end": v(44.83, 76.1) * mm, "construction": true});
            skLineSegment(sketch, "E227.0.37.0", {"start": v(26.83, 78.1) * mm, "end": v(44.83, 78.1) * mm, "construction": true});
            skLineSegment(sketch, "E227.0.38.0", {"start": v(26.83, 80.1) * mm, "end": v(44.83, 80.1) * mm, "construction": true});
            skLineSegment(sketch, "E227.0.39.0", {"start": v(26.83, 82.1) * mm, "end": v(44.83, 82.1) * mm, "construction": true});
            skLineSegment(sketch, "E227.0.40.0", {"start": v(26.83, 84.1) * mm, "end": v(44.83, 84.1) * mm, "construction": true});
            skLineSegment(sketch, "E227.0.41.0", {"start": v(26.83, 86.1) * mm, "end": v(44.83, 86.1) * mm, "construction": true});
            skLineSegment(sketch, "E227.0.42.0", {"start": v(26.83, 88.1) * mm, "end": v(44.83, 88.1) * mm, "construction": true});
            skLineSegment(sketch, "E227.0.43.0", {"start": v(26.83, 90.1) * mm, "end": v(44.83, 90.1) * mm, "construction": true});
            skLineSegment(sketch, "E227.0.44.0", {"start": v(26.83, 92.1) * mm, "end": v(44.83, 92.1) * mm, "construction": true});
            skLineSegment(sketch, "E228.1.0.0", {"start": v(27.23, 4.1) * mm, "end": v(27.23, 94.09) * mm, "construction": true});
            skLineSegment(sketch, "E228.2.0.0", {"start": v(27.63, 4.1) * mm, "end": v(27.63, 94.09) * mm, "construction": true});
            skLineSegment(sketch, "E228.3.0.0", {"start": v(28.03, 4.1) * mm, "end": v(28.03, 94.09) * mm, "construction": true});
            skLineSegment(sketch, "E228.4.0.0", {"start": v(28.43, 4.1) * mm, "end": v(28.43, 94.09) * mm, "construction": true});
            skLineSegment(sketch, "E228.5.0.0", {"start": v(28.83, 4.1) * mm, "end": v(28.83, 94.09) * mm, "construction": true});
            skLineSegment(sketch, "E228.6.0.0", {"start": v(29.23, 4.1) * mm, "end": v(29.23, 94.09) * mm, "construction": true});
            skLineSegment(sketch, "E228.7.0.0", {"start": v(29.63, 4.1) * mm, "end": v(29.63, 94.09) * mm, "construction": true});
            skLineSegment(sketch, "E228.8.0.0", {"start": v(30.03, 4.1) * mm, "end": v(30.03, 94.09) * mm, "construction": true});
            skLineSegment(sketch, "E228.9.0.0", {"start": v(30.43, 4.1) * mm, "end": v(30.43, 94.09) * mm, "construction": true});
            skLineSegment(sketch, "E228.10.0.0", {"start": v(30.83, 4.1) * mm, "end": v(30.83, 94.09) * mm, "construction": true});
            skLineSegment(sketch, "E228.11.0.0", {"start": v(31.23, 4.1) * mm, "end": v(31.23, 94.09) * mm, "construction": true});
            skLineSegment(sketch, "E228.12.0.0", {"start": v(31.63, 4.1) * mm, "end": v(31.63, 94.09) * mm, "construction": true});
            skLineSegment(sketch, "E228.13.0.0", {"start": v(32.03, 4.1) * mm, "end": v(32.03, 94.09) * mm, "construction": true});
            skLineSegment(sketch, "E228.14.0.0", {"start": v(32.43, 4.1) * mm, "end": v(32.43, 94.09) * mm, "construction": true});
            skLineSegment(sketch, "E228.15.0.0", {"start": v(32.83, 4.1) * mm, "end": v(32.83, 94.09) * mm, "construction": true});
            skLineSegment(sketch, "E228.16.0.0", {"start": v(33.23, 4.1) * mm, "end": v(33.23, 94.09) * mm, "construction": true});
            skLineSegment(sketch, "E228.17.0.0", {"start": v(33.63, 4.1) * mm, "end": v(33.63, 94.09) * mm, "construction": true});
            skLineSegment(sketch, "E228.18.0.0", {"start": v(34.03, 4.1) * mm, "end": v(34.03, 94.09) * mm, "construction": true});
            skLineSegment(sketch, "E228.19.0.0", {"start": v(34.43, 4.1) * mm, "end": v(34.43, 94.09) * mm, "construction": true});
            skLineSegment(sketch, "E228.20.0.0", {"start": v(34.83, 4.1) * mm, "end": v(34.83, 94.09) * mm, "construction": true});
            skLineSegment(sketch, "E228.21.0.0", {"start": v(35.23, 4.1) * mm, "end": v(35.23, 94.09) * mm, "construction": true});
            skLineSegment(sketch, "E228.22.0.0", {"start": v(35.63, 4.1) * mm, "end": v(35.63, 94.09) * mm, "construction": true});
            skLineSegment(sketch, "E228.23.0.0", {"start": v(36.03, 4.1) * mm, "end": v(36.03, 94.09) * mm, "construction": true});
            skLineSegment(sketch, "E228.24.0.0", {"start": v(36.43, 4.1) * mm, "end": v(36.43, 94.09) * mm, "construction": true});
            skLineSegment(sketch, "E228.25.0.0", {"start": v(36.83, 4.1) * mm, "end": v(36.83, 94.09) * mm, "construction": true});
            skLineSegment(sketch, "E228.26.0.0", {"start": v(37.23, 4.1) * mm, "end": v(37.23, 94.09) * mm, "construction": true});
            skLineSegment(sketch, "E228.27.0.0", {"start": v(37.63, 4.1) * mm, "end": v(37.63, 94.09) * mm, "construction": true});
            skLineSegment(sketch, "E228.28.0.0", {"start": v(38.03, 4.1) * mm, "end": v(38.03, 94.09) * mm, "construction": true});
            skLineSegment(sketch, "E228.29.0.0", {"start": v(38.43, 4.1) * mm, "end": v(38.43, 94.09) * mm, "construction": true});
            skLineSegment(sketch, "E228.30.0.0", {"start": v(38.83, 4.1) * mm, "end": v(38.83, 94.09) * mm, "construction": true});
            skLineSegment(sketch, "E228.31.0.0", {"start": v(39.23, 4.1) * mm, "end": v(39.23, 94.09) * mm, "construction": true});
            skLineSegment(sketch, "E228.32.0.0", {"start": v(39.63, 4.1) * mm, "end": v(39.63, 94.09) * mm, "construction": true});
            skLineSegment(sketch, "E228.33.0.0", {"start": v(40.03, 4.1) * mm, "end": v(40.03, 94.09) * mm, "construction": true});
            skLineSegment(sketch, "E228.34.0.0", {"start": v(40.43, 4.1) * mm, "end": v(40.43, 94.09) * mm, "construction": true});
            skLineSegment(sketch, "E228.35.0.0", {"start": v(40.83, 4.1) * mm, "end": v(40.83, 94.09) * mm, "construction": true});
            skLineSegment(sketch, "E228.36.0.0", {"start": v(41.23, 4.1) * mm, "end": v(41.23, 94.09) * mm, "construction": true});
            skLineSegment(sketch, "E228.37.0.0", {"start": v(41.63, 4.1) * mm, "end": v(41.63, 94.09) * mm, "construction": true});
            skLineSegment(sketch, "E228.38.0.0", {"start": v(42.03, 4.1) * mm, "end": v(42.03, 94.09) * mm, "construction": true});
            skLineSegment(sketch, "E228.39.0.0", {"start": v(42.43, 4.1) * mm, "end": v(42.43, 94.09) * mm, "construction": true});
            skLineSegment(sketch, "E228.40.0.0", {"start": v(42.83, 4.1) * mm, "end": v(42.83, 94.09) * mm, "construction": true});
            skLineSegment(sketch, "E228.41.0.0", {"start": v(43.23, 4.1) * mm, "end": v(43.23, 94.09) * mm, "construction": true});
            skLineSegment(sketch, "E228.42.0.0", {"start": v(43.63, 4.1) * mm, "end": v(43.63, 94.09) * mm, "construction": true});
            skLineSegment(sketch, "E228.43.0.0", {"start": v(44.03, 4.1) * mm, "end": v(44.03, 94.09) * mm, "construction": true});
            skLineSegment(sketch, "E228.44.0.0", {"start": v(44.43, 4.1) * mm, "end": v(44.43, 94.09) * mm, "construction": true});
            skLineSegment(sketch, "E228.direction1", {"start": v(26.83, 4.1) * mm, "end": v(27.23, 4.1) * mm, "construction": true});
            skLineSegment(sketch, "E229.bottom", {"start": v(26.83, 94.09) * mm, "end": v(44.84, 94.09) * mm});
            skLineSegment(sketch, "E229.top", {"start": v(26.83, 4.1) * mm, "end": v(44.84, 4.1) * mm});
            skLineSegment(sketch, "E229.left", {"start": v(26.83, 94.09) * mm, "end": v(26.83, 4.1) * mm});
            skLineSegment(sketch, "E229.right", {"start": v(44.84, 94.09) * mm, "end": v(44.84, 4.1) * mm});
            skLineSegment(sketch, "E230.bottom", {"start": v(26.83, 4.1) * mm, "end": v(24.83, 4.1) * mm});
            skLineSegment(sketch, "E230.top", {"start": v(26.83, 94.1) * mm, "end": v(24.83, 94.1) * mm});
            skLineSegment(sketch, "E230.left", {"start": v(26.83, 4.1) * mm, "end": v(26.83, 94.1) * mm});
            skLineSegment(sketch, "E230.right", {"start": v(24.83, 4.1) * mm, "end": v(24.83, 94.1) * mm});
            skSolve(sketch);
        }
        {
            var Q0;
            Q0=makeQuery(id+"F6.imprint","IMPRINT",FACE,{"disambiguationData":[TD([[makeQuery(id+"F6.imprint","IMPRINT",EDGE,{"derivedFrom":sQuery(id+"F6.wireOp",EDGE,"E229.bottom")}),-1.0]])]});
            extrude(context, id + "F7", {"entities" : qUnion([Q0]), "oppositeDirection" : true, "depth" : 25.4 * mm, "offsetDistance" : 25.4 * mm});
        }
        {
            var Q0;
            {var subQ3=sQuery(id+"F6.wireOp",EDGE,"E230.bottom");Q0=makeQuery(id+"F6.imprint","IMPRINT",FACE,{"disambiguationData":[TD([[makeQuery(id+"F6.imprint","IMPRINT",EDGE,{"derivedFrom":subQ3}),-1.0]])]});}
            extrude(context, id + "F8", {"entities" : qUnion([Q0]), "oppositeDirection" : true, "depth" : 25.4 * mm, "offsetDistance" : 25.4 * mm});
        }
    });
